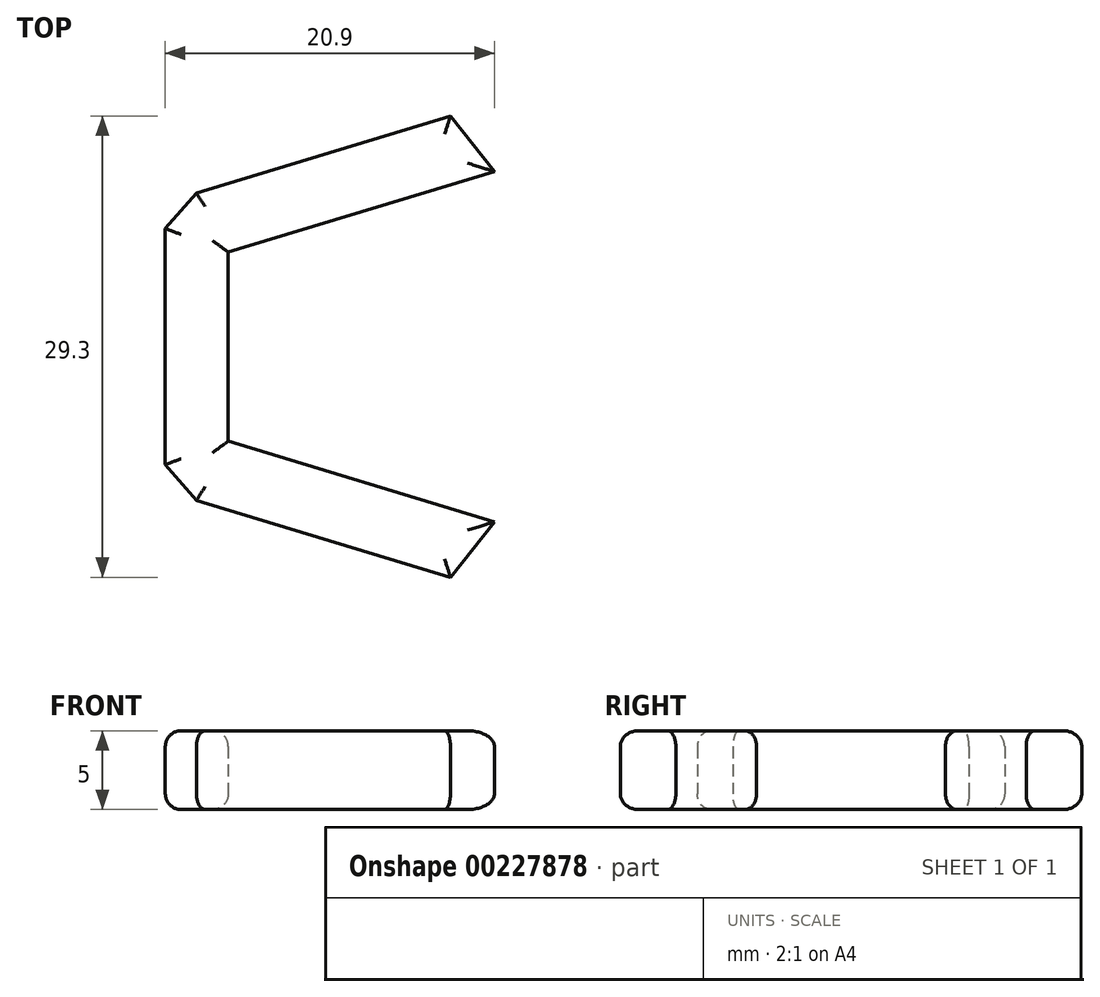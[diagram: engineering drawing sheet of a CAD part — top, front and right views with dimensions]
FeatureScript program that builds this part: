
annotation { "Feature Type Name" : "Feature", "Feature Type Description" : "" }
export const myFeature = defineFeature(function(context is Context, id is Id, definition is map)
    precondition{}
    {
        {
            var Q0;
            Q0=qCreatedBy(makeId("Top.planeOp"),FACE);
            cPlane(context, id + "F0", {"entities" : qUnion([Q0]), "cplaneType" : CPlaneType.OFFSET, "offset" : 44 * mm, "width" : 150 * mm, "height" : 150 * mm});
        }
        {
            var Q0;
            Q0=qCreatedBy(id+"F0.planeOp",FACE);
            var sketch = newSketch(context, id + "F1", { "sketchPlane" : qUnion([Q0])});
            skLineSegment(sketch, "E0", {"start": v(0, 0) * mm, "end": v(-16.9, 0) * mm, "construction": true});
            skLineSegment(sketch, "E1", {"start": v(-16.9, 0) * mm, "end": v(-16.9, 6) * mm});
            skLineSegment(sketch, "E2.MirrorCS", {"start": v(-16.9, 0) * mm, "end": v(-16.9, -6) * mm});
            skLineSegment(sketch, "E3", {"start": v(0, 0) * mm, "end": v(0, 11.12) * mm, "construction": true});
            skLineSegment(sketch, "E4", {"start": v(-16.9, 0) * mm, "end": v(-20.9, 0) * mm, "construction": true});
            skLineSegment(sketch, "E5", {"start": v(-2.8, 14.65) * mm, "end": v(-18.93, 9.76) * mm});
            skLineSegment(sketch, "E6", {"start": v(-18.93, 9.76) * mm, "end": v(-20.9, 7.5) * mm});
            skLineSegment(sketch, "E7", {"start": v(-20.9, 7.5) * mm, "end": v(-20.9, 0) * mm});
            skLineSegment(sketch, "E8", {"start": v(-20.9, 7.5) * mm, "end": v(-19.91, 8.63) * mm});
            skLineSegment(sketch, "E9", {"start": v(-20.9, 7.5) * mm, "end": v(-16.9, 6) * mm, "construction": true});
            skLineSegment(sketch, "E10", {"start": v(-16.9, 6) * mm, "end": v(-18.93, 9.76) * mm, "construction": true});
            skLineSegment(sketch, "E11", {"start": v(-16.9, 6) * mm, "end": v(0, 11.12) * mm});
            skLineSegment(sketch, "E12", {"start": v(0, 15.5) * mm, "end": v(0, 11.12) * mm});
            skLineSegment(sketch, "E13", {"start": v(-16.9, 0) * mm, "end": v(-20.9, 0) * mm});
            skPoint(sketch, "E14.visualSharp", {"position": v(0, 15.5) * mm});
            skLineSegment(sketch, "E15", {"start": v(-2.8, 14.65) * mm, "end": v(0, 11.12) * mm});
            skSolve(sketch);
        }
        {
            var Q0;
            Q0=makeQuery(id+"F1.imprint","IMPRINT",FACE,{"disambiguationData":[TD([[makeQuery(id+"F1.imprint","IMPRINT",EDGE,{"derivedFrom":sQuery(id+"F1.wireOp",EDGE,"E1")}),1.0]])]});
            extrude(context, id + "F2", {"entities" : qUnion([Q0]), "depth" : 2.5 * mm, "hasSecondDirection" : true, "secondDirectionOppositeDirection" : true, "secondDirectionDepth" : 2.5 * mm});
        }
        {
            var Q0;
            Q0=makeQuery(id+"F2.opExtrude","SWEPT_BODY",BODY,{"disambiguationData":[OSD([sQuery(id+"F1.wireOp",EDGE,"E1"),sQuery(id+"F1.wireOp",EDGE,"E5"),sQuery(id+"F1.wireOp",EDGE,"E6"),sQuery(id+"F1.wireOp",EDGE,"E7"),sQuery(id+"F1.wireOp",EDGE,"E8"),sQuery(id+"F1.wireOp",EDGE,"E11"),sQuery(id+"F1.wireOp",EDGE,"E12"),sQuery(id+"F1.wireOp",EDGE,"E13")])]});
            var Q1;
            Q1=qCreatedBy(makeId("Front.planeOp"),FACE);
            mirror(context, id + "F3", {"operationType" : NewBodyOperationType.ADD, "entities" : qUnion([Q0]), "mirrorPlane" : qUnion([Q1])});
        }
        {
            var Q0;
            Q0=makeQuery(id+"F2.opExtrude","CAP_FACE",FACE,{"disambiguationData":[OSD([sQuery(id+"F1.wireOp",EDGE,"E1"),sQuery(id+"F1.wireOp",EDGE,"E2.MirrorCS"),sQuery(id+"F1.wireOp",EDGE,"f9sqKp3z-0CHV-07Te-Oeja-OX5G6zjyapWy"),sQuery(id+"F1.wireOp",EDGE,"j632fLxQ-Wrsb-5NP3-qyab-8AJ86kqfrhG6"),sQuery(id+"F1.wireOp",EDGE,"ojiIwMsm-85lX-pom6-riJS-mGGJFQGc8e1p"),sQuery(id+"F1.wireOp",EDGE,"Y682RtV5-OXSZ-7dt5-VdsK-hqfnQB1xatHe"),sQuery(id+"F1.wireOp",EDGE,"8887cd48-202b-4fe8-b272-4e11588c50af.trimOffspring")])],"isStart":false});
            var Q1;
            Q1=makeQuery(id+"F2.opExtrude","CAP_FACE",FACE,{"disambiguationData":[OSD([sQuery(id+"F1.wireOp",EDGE,"E1"),sQuery(id+"F1.wireOp",EDGE,"E2.MirrorCS"),sQuery(id+"F1.wireOp",EDGE,"f9sqKp3z-0CHV-07Te-Oeja-OX5G6zjyapWy"),sQuery(id+"F1.wireOp",EDGE,"j632fLxQ-Wrsb-5NP3-qyab-8AJ86kqfrhG6"),sQuery(id+"F1.wireOp",EDGE,"ojiIwMsm-85lX-pom6-riJS-mGGJFQGc8e1p"),sQuery(id+"F1.wireOp",EDGE,"Y682RtV5-OXSZ-7dt5-VdsK-hqfnQB1xatHe"),sQuery(id+"F1.wireOp",EDGE,"8887cd48-202b-4fe8-b272-4e11588c50af.trimOffspring")])],"isStart":true});
            fillet(context, id + "F4", {"entities" : qUnion([Q0, Q1]), "radius" : 1 * mm, "tangentPropagation" : true, "allowEdgeOverflow" : false});
        }
    });
